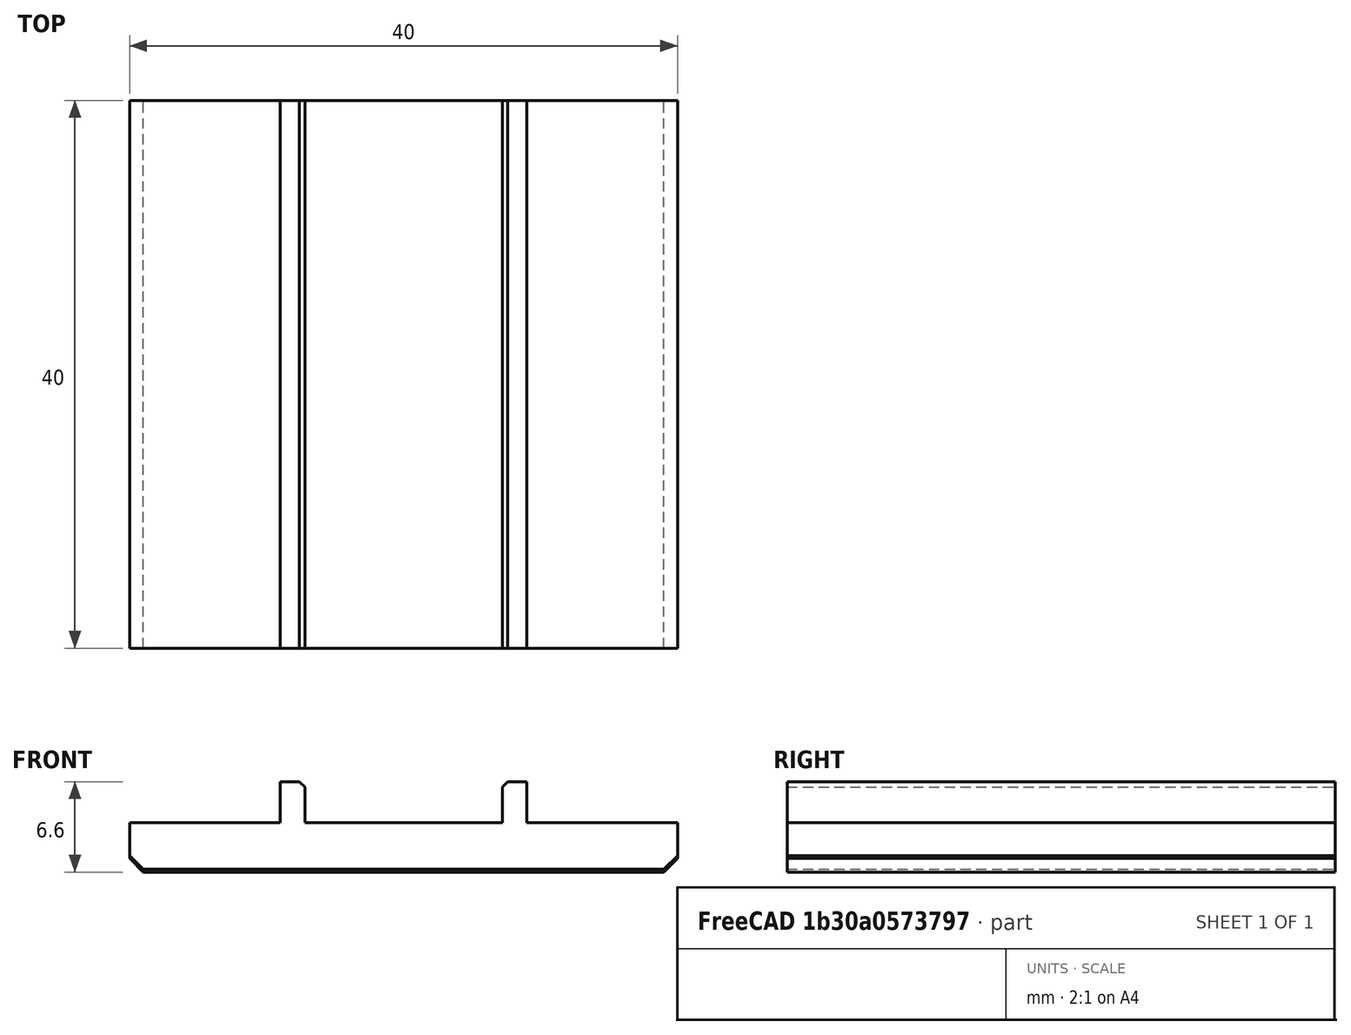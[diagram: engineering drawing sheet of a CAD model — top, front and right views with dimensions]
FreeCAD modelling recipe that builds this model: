
FCSTD DOCUMENT  (FreeCAD 0.18R16146 (Git))
Label: z-motor-supporter
License: All rights reserved
LicenseURL: http://en.wikipedia.org/wiki/All_rights_reserved
objects: Part::Box×4, Part::Chamfer×4, Part::Feature×2, Part::MultiFuse×2
note: 12 computed .brp shape members not serialized (recipe doc carries the construction recipe); baked Part::Feature solids carry a one-line shape summary decoded from their .brp

FEATURE [Part::Box] Box  label="Cube"
  AttacherType = Attacher::AttachEngine3D
  Height = 3.6
  Length = 40
  Placement = pos=(-20,0,-3.6) rot=(0,0,1;0rad)
  Width = 40
FEATURE [Part::Box] Box001  label="Cube001"
  AttacherType = Attacher::AttachEngine3D
  Height = 3
  Length = 1.8
  Placement = pos=(-9,0,0) rot=(0,0,1;0rad)
  Width = 40
FEATURE [Part::Box] Box002  label="Cube002"
  AttacherType = Attacher::AttachEngine3D
  Height = 3
  Length = 1.8
  Placement = pos=(7.2,0,0) rot=(0,0,1;0rad)
  Width = 40
FEATURE [Part::Chamfer] Chamfer
  Base = -> Box001
  Edges = 1 edges r=0.4: [Edge6]
FEATURE [Part::Chamfer] Chamfer001
  Base = -> Box002
  Edges = 1 edges r=0.4: [Edge2]
FEATURE [Part::Box] Box003  label="Cube003"
  AttacherType = Attacher::AttachEngine3D
  Height = 3.4
  Length = 40
  Placement = pos=(-20,0,-3.4) rot=(0,0,1;0rad)
  Width = 40
FEATURE [Part::Feature] Chamfer002
  shape: bbox 1.8 x 40 x 3 mm, 7 faces (baked)
FEATURE [Part::Feature] Chamfer001001  label="Chamfer003"
  shape: bbox 1.8 x 40 x 3 mm, 7 faces (baked)
FEATURE [Part::MultiFuse] Fusion001
  Shapes = -> [Chamfer002,Chamfer001001,Box003]
FEATURE [Part::Chamfer] Chamfer001002
  Base = -> Fusion001
  Edges = 2 edges r=1: [Edge4,Edge20]
FEATURE [Part::Chamfer] Chamfer001003
  Base = -> Box
  Edges = 2 edges r=1: [Edge4,Edge8]
FEATURE [Part::MultiFuse] Fusion
  Shapes = -> [Chamfer001003,Chamfer001,Chamfer]
